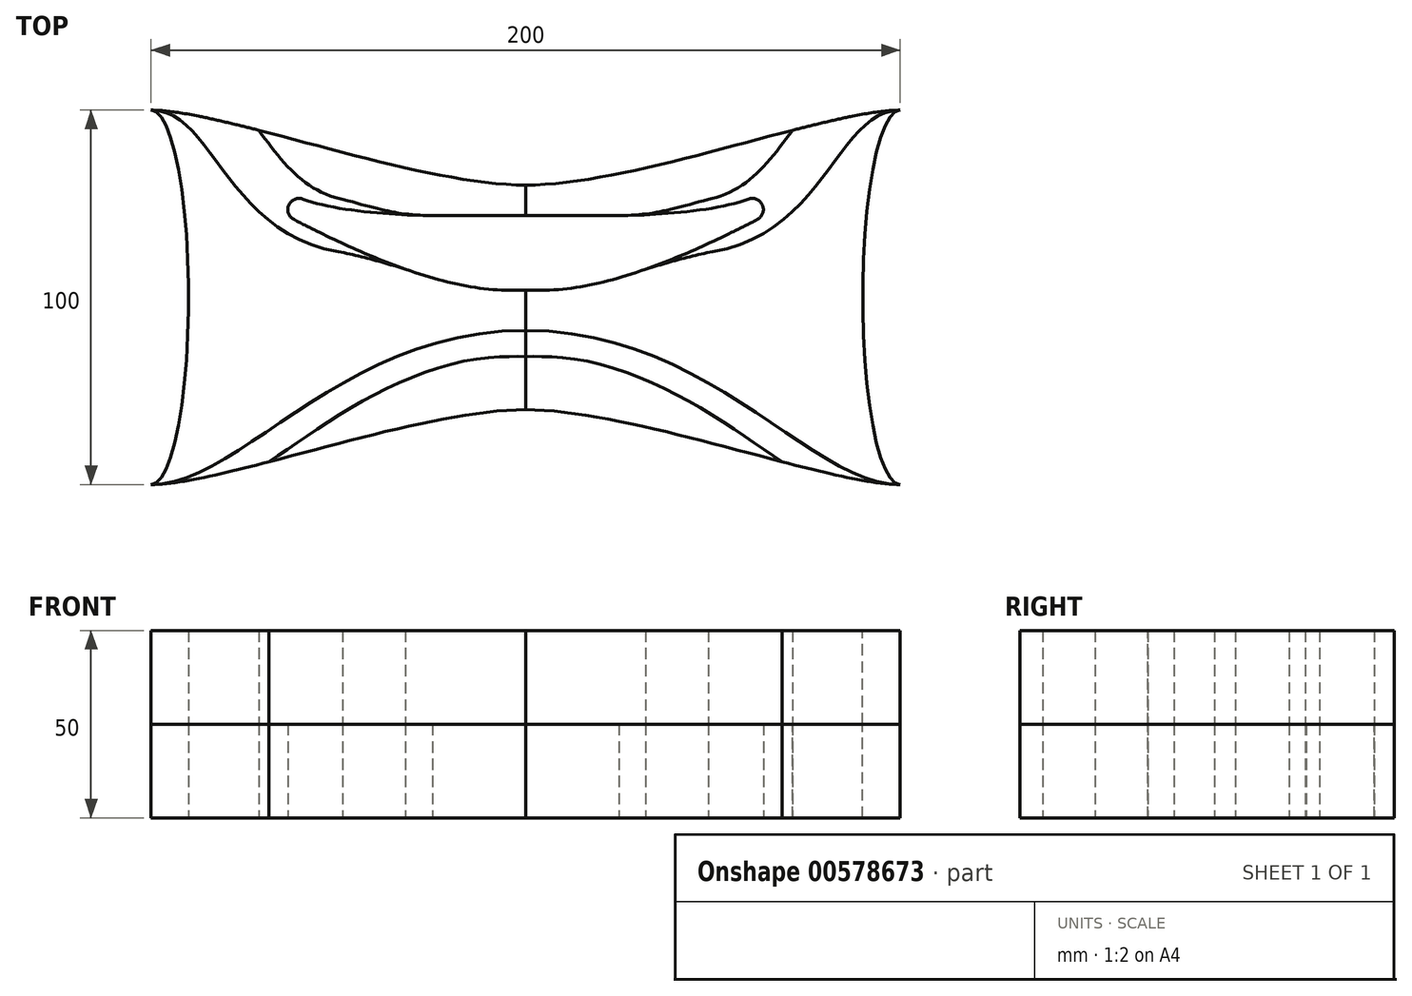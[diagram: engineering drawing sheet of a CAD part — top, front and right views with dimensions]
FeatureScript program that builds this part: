
annotation { "Feature Type Name" : "Feature", "Feature Type Description" : "" }
export const myFeature = defineFeature(function(context is Context, id is Id, definition is map)
    precondition{}
    {
        {
            var Q0;
            Q0=qCreatedBy(makeId("Top.planeOp"),FACE);
            var sketch = newSketch(context, id + "F0", { "sketchPlane" : qUnion([Q0])});
            skFitSpline(sketch, "E0", {"points": [v(-100, 30) * mm, v(0, 50) * mm], "startDerivative": vector(87.46, 0) * mm, "endDerivative": vector(57.85, 0) * mm});
            skLineSegment(sketch, "E1", {"start": v(-100, 30) * mm, "end": v(-100, -30) * mm});
            skLineSegment(sketch, "E2", {"start": v(0, 50) * mm, "end": v(0, -50) * mm});
            skFitSpline(sketch, "E3", {"points": [v(-100, -30) * mm, v(0, -50) * mm], "startDerivative": vector(87.46, 0) * mm, "endDerivative": vector(57.85, 0) * mm});
            skPoint(sketch, "E4.1.internal.snap0", {"position": v(0, 0) * mm});
            skEllipse(sketch, "E5", {"center": v(0, 0) * mm, "majorRadius": 50 * mm, "minorRadius": 10 * mm, "majorAxis": v(0, 1)});
            skFitSpline(sketch, "E6", {"points": [v(0, -50) * mm, v(-100, -8.83) * mm], "startDerivative": vector(-72.2, 0) * mm, "endDerivative": vector(-147.65, 0) * mm});
            skFitSpline(sketch, "E7.0", {"points": [v(0, -57) * mm, v(-2, -57) * mm, v(-5.95, -56.57) * mm, v(-11.6, -54.94) * mm, v(-17.03, -52.58) * mm, v(-22.37, -49.69) * mm, v(-27.7, -46.4) * mm, v(-34.91, -41.63) * mm, v(-44.24, -35.25) * mm, v(-56.27, -27.8) * mm, v(-69.35, -21.46) * mm, v(-83.7, -17) * mm, v(-94.34, -15.83) * mm, v(-100, -15.83) * mm]});
            skFitSpline(sketch, "E8", {"points": [v(0, 50) * mm, v(-50, 12.18) * mm], "startDerivative": vector(-49.8, 0) * mm, "endDerivative": vector(-90.4, -15.84) * mm});
            skFitSpline(sketch, "E9", {"points": [v(-50, 12.18) * mm, v(-95.83, 1.88) * mm], "startDerivative": vector(-44.68, -7.83) * mm, "endDerivative": vector(-44.3, 0) * mm});
            skFitSpline(sketch, "E10.0", {"points": [v(0, 64) * mm, v(-1.1, 64) * mm, v(-3.27, 63.87) * mm, v(-6.44, 63.26) * mm, v(-9.43, 62.3) * mm, v(-12.17, 61.05) * mm, v(-14.63, 59.6) * mm, v(-17.55, 57.5) * mm, v(-20.62, 54.7) * mm, v(-23.66, 51.3) * mm, v(-26.32, 47.92) * mm, v(-28.76, 44.64) * mm, v(-31.1, 41.49) * mm, v(-33.39, 38.52) * mm, v(-35.7, 35.8) * mm, v(-38.05, 33.37) * mm, v(-40.47, 31.25) * mm, v(-43, 29.46) * mm, v(-45.72, 27.97) * mm, v(-48.77, 26.78) * mm, v(-51.12, 26.2) * mm, v(-52.42, 25.97) * mm]});
            skFitSpline(sketch, "E11", {"points": [v(-50, 26.5) * mm, v(-75.46, 21.88) * mm], "startDerivative": vector(-34.45, -9.14) * mm, "endDerivative": vector(-28.65, 0.1) * mm});
            skLineSegment(sketch, "E12", {"start": v(-75.15, 21.88) * mm, "end": v(-100, 21.88) * mm});
            skLineSegment(sketch, "E13", {"start": v(-95.83, 1.88) * mm, "end": v(-100, 1.88) * mm});
            skFitSpline(sketch, "E14.0", {"points": [v(0, 57) * mm, v(-0.8, 57) * mm, v(-2.4, 56.9) * mm, v(-4.71, 56.46) * mm, v(-6.9, 55.76) * mm, v(-9.6, 54.53) * mm, v(-12.58, 52.56) * mm, v(-15.6, 49.8) * mm, v(-18.27, 46.82) * mm, v(-20.74, 43.7) * mm, v(-23.12, 40.5) * mm, v(-26.29, 36.21) * mm, v(-29.58, 32.06) * mm, v(-33.2, 28.31) * mm, v(-36.1, 25.76) * mm, v(-39.27, 23.51) * mm, v(-42.76, 21.6) * mm, v(-46.66, 20.08) * mm, v(-49.62, 19.35) * mm, v(-51.2, 19.07) * mm], "construction": true});
            skCircle(sketch, "E15", {"center": v(-39.51, 23.45) * mm, "radius": 3 * mm});
            skFitSpline(sketch, "E16.0", {"points": [v(0, 54) * mm, v(-1.36, 54) * mm, v(-4.02, 53.66) * mm, v(-7.6, 52.25) * mm, v(-10.7, 50.2) * mm, v(-13.45, 47.7) * mm, v(-15.96, 44.9) * mm, v(-19.14, 40.88) * mm, v(-23.04, 35.48) * mm, v(-28.14, 29.04) * mm, v(-33.09, 24.22) * mm, v(-37.67, 20.96) * mm, v(-42.76, 18.18) * mm, v(-47.26, 16.72) * mm, v(-50.7, 16.12) * mm]});
            skFitSpline(sketch, "E17.0", {"points": [v(0, 60) * mm, v(-0.93, 60) * mm, v(-2.77, 59.89) * mm, v(-5.45, 59.38) * mm, v(-7.98, 58.56) * mm, v(-10.31, 57.5) * mm, v(-12.44, 56.25) * mm, v(-15, 54.42) * mm, v(-17.75, 51.9) * mm, v(-20.58, 48.74) * mm, v(-23.13, 45.5) * mm, v(-25.54, 42.27) * mm, v(-28.68, 38.02) * mm, v(-31.86, 34.01) * mm, v(-35.27, 30.48) * mm, v(-37.97, 28.11) * mm, v(-40.87, 26.06) * mm, v(-44.03, 24.33) * mm, v(-47.56, 22.95) * mm, v(-50.27, 22.28) * mm, v(-51.73, 22.03) * mm]});
            skFitSpline(sketch, "E18", {"points": [v(-75.15, 21.88) * mm, v(-40.61, 26.24) * mm], "startDerivative": vector(25.9, 0) * mm, "endDerivative": vector(25.1, 9.89) * mm});
            skFitSpline(sketch, "E19", {"points": [v(-38.13, 20.79) * mm, v(-95.83, 1.88) * mm], "startDerivative": vector(-54.64, -28.3) * mm, "endDerivative": vector(-52.77, 0) * mm});
            skLineSegment(sketch, "E20", {"start": v(-50, 26.5) * mm, "end": v(-50, 12.18) * mm, "construction": true});
            skPoint(sketch, "E21", {"position": v(-100, 0) * mm});
            skSolve(sketch);
        }
        {
            var Q0;
            {var subQ0=sQuery(id+"F0.wireOp",EDGE,"E11");Q0=makeQuery(id+"F0.imprint","IMPRINT",FACE,{"disambiguationData":[TD([[makeQuery(id+"F0.imprint","IMPRINT",EDGE,{"derivedFrom":subQ0}),-1.0]])]});}
            var Q1;
            {var subQ0=sQuery(id+"F0.wireOp",EDGE,"E6");Q1=makeQuery(id+"F0.imprint","IMPRINT",FACE,{"disambiguationData":[TD([[makeQuery(id+"F0.imprint","IMPRINT",EDGE,{"derivedFrom":subQ0}),-1.0]])]});}
            var Q2;
            {var subQ0=sQuery(id+"F0.wireOp",EDGE,"E3");var subQ1=sQuery(id+"F0.wireOp",EDGE,"E1");var subQ2=makeQuery(id+"F0.imprint","INTERSECT",VERTEX,{"derivedFrom":[subQ1,subQ0]});Q2=makeQuery(id+"F0.imprint","IMPRINT",FACE,{"disambiguationData":[TD([[makeQuery(id+"F0.imprint","IMPRINT",EDGE,{"disambiguationData":[TD([[subQ2,1.0]])],"derivedFrom":subQ1}),1.0]])]});}
            extrude(context, id + "F1", {"entities" : qUnion([Q0, Q1, Q2]), "depth" : 25 * mm, "offsetDistance" : 25 * mm});
        }
        {
            var Q0;
            Q0=makeQuery(id+"F1.opExtrude","CAP_FACE",FACE,{"disambiguationData":[OSD([sQuery(id+"F0.wireOp",EDGE,"E0"),sQuery(id+"F0.wireOp",EDGE,"E1"),sQuery(id+"F0.wireOp",EDGE,"E10.0"),sQuery(id+"F0.wireOp",EDGE,"E11"),sQuery(id+"F0.wireOp",EDGE,"E12")])],"isStart":false});
            var Q1;
            {var subQ0=sQuery(id+"F0.wireOp",EDGE,"E11");Q1=makeQuery(id+"F0.imprint","IMPRINT",FACE,{"disambiguationData":[TD([[makeQuery(id+"F0.imprint","IMPRINT",EDGE,{"derivedFrom":subQ0}),1.0]])]});}
            var Q2;
            {var subQ1=sQuery(id+"F0.wireOp",EDGE,"E8");Q2=makeQuery(id+"F0.imprint","IMPRINT",FACE,{"disambiguationData":[TD([[makeQuery(id+"F0.imprint","IMPRINT",EDGE,{"derivedFrom":subQ1}),-1.0]])]});}
            var Q3;
            Q3=makeQuery(id+"F1.opExtrude","CAP_FACE",FACE,{"disambiguationData":[OSD([sQuery(id+"F0.wireOp",EDGE,"E1"),sQuery(id+"F0.wireOp",EDGE,"E5"),sQuery(id+"F0.wireOp",EDGE,"E6"),sQuery(id+"F0.wireOp",EDGE,"E8"),sQuery(id+"F0.wireOp",EDGE,"E9"),sQuery(id+"F0.wireOp",EDGE,"E13"),sQuery(id+"F0.wireOp",EDGE,"E19")])],"isStart":false});
            var Q4;
            Q4=makeQuery(id+"F1.opExtrude","CAP_FACE",FACE,{"disambiguationData":[OSD([sQuery(id+"F0.wireOp",EDGE,"E1"),sQuery(id+"F0.wireOp",EDGE,"E3"),sQuery(id+"F0.wireOp",EDGE,"E7.0")])],"isStart":false});
            var Q5;
            {var subQ0=sQuery(id+"F0.wireOp",EDGE,"E6");Q5=makeQuery(id+"F0.imprint","IMPRINT",FACE,{"disambiguationData":[TD([[makeQuery(id+"F0.imprint","IMPRINT",EDGE,{"derivedFrom":subQ0}),1.0]])]});}
            var Q6;
            {var subQ0=sQuery(id+"F0.wireOp",EDGE,"E17.0");var subQ1=sQuery(id+"F0.wireOp",EDGE,"E0");var subQ2=makeQuery(id+"F0.imprint","INTERSECT",VERTEX,{"derivedFrom":[subQ1,subQ0]});Q6=makeQuery(id+"F0.imprint","IMPRINT",FACE,{"disambiguationData":[TD([[makeQuery(id+"F0.imprint","IMPRINT",EDGE,{"disambiguationData":[TD([[subQ2,-1.0]])],"derivedFrom":subQ1}),-1.0]])]});}
            extrude(context, id + "F2", {"entities" : qUnion([Q0, Q1, Q2, Q3, Q4, Q5, Q6]), "depth" : 25 * mm, "offsetDistance" : 25 * mm});
        }
        {
            var Q0;
            Q0=makeQuery(id+"F2.opExtrude","SWEPT_BODY",BODY,{"disambiguationData":[OSD([sQuery(id+"F0.wireOp",EDGE,"E0"),sQuery(id+"F0.wireOp",EDGE,"E8"),sQuery(id+"F0.wireOp",EDGE,"E9"),sQuery(id+"F0.wireOp",EDGE,"E10.0"),sQuery(id+"F0.wireOp",EDGE,"E11"),sQuery(id+"F0.wireOp",EDGE,"E15"),sQuery(id+"F0.wireOp",EDGE,"E16.0"),sQuery(id+"F0.wireOp",EDGE,"E18"),sQuery(id+"F0.wireOp",EDGE,"E19")])]});
            var Q1;
            Q1=makeQuery(id+"F2.opExtrude","SWEPT_BODY",BODY,{"disambiguationData":[OSD([sQuery(id+"F0.wireOp",EDGE,"E1"),sQuery(id+"F0.wireOp",EDGE,"E3"),sQuery(id+"F0.wireOp",EDGE,"E6"),sQuery(id+"F0.wireOp",EDGE,"E7.0")])]});
            var Q2;
            Q2=makeQuery(id+"F1.opExtrude","SWEPT_BODY",BODY,{"disambiguationData":[OSD([sQuery(id+"F0.wireOp",EDGE,"E0"),sQuery(id+"F0.wireOp",EDGE,"E1"),sQuery(id+"F0.wireOp",EDGE,"E10.0"),sQuery(id+"F0.wireOp",EDGE,"E11"),sQuery(id+"F0.wireOp",EDGE,"E12")])]});
            var Q3;
            Q3=makeQuery(id+"F1.opExtrude","SWEPT_BODY",BODY,{"disambiguationData":[OSD([sQuery(id+"F0.wireOp",EDGE,"E1"),sQuery(id+"F0.wireOp",EDGE,"E5"),sQuery(id+"F0.wireOp",EDGE,"E6"),sQuery(id+"F0.wireOp",EDGE,"E8"),sQuery(id+"F0.wireOp",EDGE,"E9"),sQuery(id+"F0.wireOp",EDGE,"E13"),sQuery(id+"F0.wireOp",EDGE,"E19")])]});
            var Q4;
            Q4=makeQuery(id+"F1.opExtrude","SWEPT_BODY",BODY,{"disambiguationData":[OSD([sQuery(id+"F0.wireOp",EDGE,"E1"),sQuery(id+"F0.wireOp",EDGE,"E3"),sQuery(id+"F0.wireOp",EDGE,"E7.0")])]});
            var Q5;
            Q5=makeQuery(id+"F2.opExtrude","SWEPT_BODY",BODY,{"disambiguationData":[OSD([sQuery(id+"F0.wireOp",EDGE,"E0"),sQuery(id+"F0.wireOp",EDGE,"E1"),sQuery(id+"F0.wireOp",EDGE,"E10.0"),sQuery(id+"F0.wireOp",EDGE,"E11"),sQuery(id+"F0.wireOp",EDGE,"E12")])]});
            var Q6;
            Q6=makeQuery(id+"F2.opExtrude","SWEPT_BODY",BODY,{"disambiguationData":[OSD([sQuery(id+"F0.wireOp",EDGE,"E1"),sQuery(id+"F0.wireOp",EDGE,"E5"),sQuery(id+"F0.wireOp",EDGE,"E6"),sQuery(id+"F0.wireOp",EDGE,"E8"),sQuery(id+"F0.wireOp",EDGE,"E9"),sQuery(id+"F0.wireOp",EDGE,"E13"),sQuery(id+"F0.wireOp",EDGE,"E19")])]});
            var Q7;
            Q7=makeQuery(id+"F2.opExtrude","SWEPT_BODY",BODY,{"disambiguationData":[OSD([sQuery(id+"F0.wireOp",EDGE,"E1"),sQuery(id+"F0.wireOp",EDGE,"E3"),sQuery(id+"F0.wireOp",EDGE,"E7.0")])]});
            var Q8;
            {var subQ0=sQuery(id+"F0.wireOp",EDGE,"E1");Q8=makeQuery(id+"F1.opExtrude","SWEPT_FACE",FACE,{"disambiguationData":[OSD([subQ0]),TDD([makeQuery(id+"F0.imprint","IMPRINT",EDGE,{"disambiguationData":[TD([[makeQuery(id+"F0.imprint","INTERSECT",VERTEX,{"derivedFrom":[subQ0,sQuery(id+"F0.wireOp",EDGE,"E6")]}),1.0]])],"derivedFrom":subQ0})])]});}
            mirror(context, id + "F3", {"entities" : qUnion([Q0, Q1, Q2, Q3, Q4, Q5, Q6, Q7]), "mirrorPlane" : qUnion([Q8])});
        }
    });
